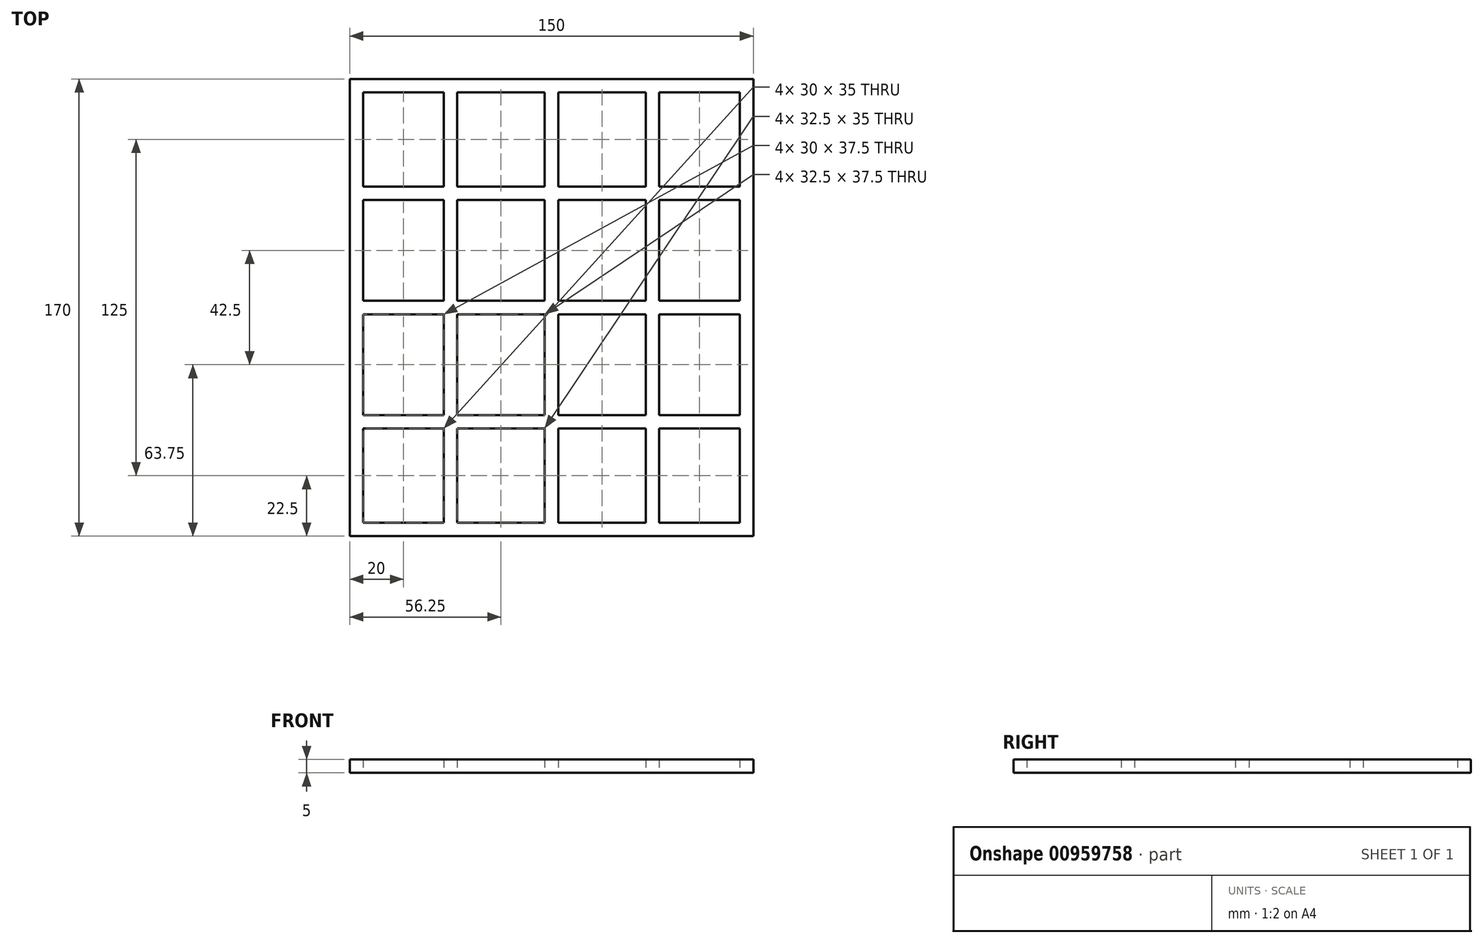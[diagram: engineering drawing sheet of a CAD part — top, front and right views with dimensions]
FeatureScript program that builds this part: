
annotation { "Feature Type Name" : "Feature", "Feature Type Description" : "" }
export const myFeature = defineFeature(function(context is Context, id is Id, definition is map)
    precondition{}
    {
        {
            var Q0;
            Q0=qCreatedBy(makeId("Top.planeOp"),FACE);
            var sketch = newSketch(context, id + "F0", { "sketchPlane" : qUnion([Q0])});
            skLineSegment(sketch, "E0.bottom", {"start": v(-107, 117) * mm, "end": v(107, 117) * mm});
            skLineSegment(sketch, "E0.top", {"start": v(-107, -117) * mm, "end": v(107, -117) * mm});
            skLineSegment(sketch, "E0.left", {"start": v(-107, 117) * mm, "end": v(-107, -117) * mm});
            skLineSegment(sketch, "E0.right", {"start": v(107, 117) * mm, "end": v(107, -117) * mm});
            skLineSegment(sketch, "E1.0", {"start": v(-75, 85) * mm, "end": v(-37.5, 85) * mm});
            skLineSegment(sketch, "E1.1", {"start": v(-75, 85) * mm, "end": v(-75, 42.5) * mm});
            skLineSegment(sketch, "E1.2", {"start": v(-75, -85) * mm, "end": v(-37.5, -85) * mm});
            skLineSegment(sketch, "E1.3", {"start": v(75, 85) * mm, "end": v(75, 42.5) * mm});
            skLineSegment(sketch, "E2", {"start": v(-75, 0) * mm, "end": v(-75, -42.5) * mm});
            skLineSegment(sketch, "E3", {"start": v(75, 0) * mm, "end": v(75, -42.5) * mm});
            skLineSegment(sketch, "E4", {"start": v(0, 85) * mm, "end": v(37.5, 85) * mm});
            skLineSegment(sketch, "E5", {"start": v(0, -85) * mm, "end": v(37.5, -85) * mm});
            skLineSegment(sketch, "E6", {"start": v(-37.5, -85) * mm, "end": v(0, -85) * mm});
            skLineSegment(sketch, "E7", {"start": v(37.5, -85) * mm, "end": v(75, -85) * mm});
            skLineSegment(sketch, "E8", {"start": v(75, 42.5) * mm, "end": v(75, 0) * mm});
            skLineSegment(sketch, "E9", {"start": v(75, -42.5) * mm, "end": v(75, -85) * mm});
            skLineSegment(sketch, "E10", {"start": v(-75, 42.5) * mm, "end": v(-75, 0) * mm});
            skLineSegment(sketch, "E11", {"start": v(-75, -42.5) * mm, "end": v(-75, -85) * mm});
            skLineSegment(sketch, "E12", {"start": v(37.5, 85) * mm, "end": v(75, 85) * mm});
            skLineSegment(sketch, "E13", {"start": v(-37.5, 85) * mm, "end": v(0, 85) * mm});
            skLineSegment(sketch, "E14.0", {"start": v(-70, 80) * mm, "end": v(-70, 45) * mm});
            skLineSegment(sketch, "E14.1", {"start": v(-70, 40) * mm, "end": v(-70, 2.5) * mm});
            skLineSegment(sketch, "E14.2", {"start": v(-70, -2.5) * mm, "end": v(-70, -40) * mm});
            skLineSegment(sketch, "E14.3", {"start": v(-70, -45) * mm, "end": v(-70, -80) * mm});
            skLineSegment(sketch, "E14.4", {"start": v(-70, -80) * mm, "end": v(-40, -80) * mm});
            skLineSegment(sketch, "E14.5", {"start": v(70, 80) * mm, "end": v(70, 45) * mm});
            skLineSegment(sketch, "E14.6", {"start": v(40, 80) * mm, "end": v(70, 80) * mm});
            skLineSegment(sketch, "E14.7", {"start": v(2.5, 80) * mm, "end": v(35, 80) * mm});
            skLineSegment(sketch, "E14.8", {"start": v(-35, 80) * mm, "end": v(-2.5, 80) * mm});
            skLineSegment(sketch, "E14.9", {"start": v(70, 40) * mm, "end": v(70, 2.5) * mm});
            skLineSegment(sketch, "E14.10", {"start": v(70, -2.5) * mm, "end": v(70, -40) * mm});
            skLineSegment(sketch, "E14.11", {"start": v(70, -45) * mm, "end": v(70, -80) * mm});
            skLineSegment(sketch, "E14.12", {"start": v(40, -80) * mm, "end": v(70, -80) * mm});
            skLineSegment(sketch, "E14.13", {"start": v(2.5, -80) * mm, "end": v(35, -80) * mm});
            skLineSegment(sketch, "E14.14", {"start": v(-70, 80) * mm, "end": v(-40, 80) * mm});
            skLineSegment(sketch, "E14.15", {"start": v(-35, -80) * mm, "end": v(-2.5, -80) * mm});
            skLineSegment(sketch, "E15.0", {"start": v(-40, -45) * mm, "end": v(-40, -80) * mm});
            skLineSegment(sketch, "E15.1", {"start": v(-40, -2.5) * mm, "end": v(-40, -40) * mm});
            skLineSegment(sketch, "E15.2", {"start": v(-40, 40) * mm, "end": v(-40, 2.5) * mm});
            skLineSegment(sketch, "E15.3", {"start": v(-40, 80) * mm, "end": v(-40, 45) * mm});
            skLineSegment(sketch, "E16.0", {"start": v(-35, -45) * mm, "end": v(-35, -80) * mm});
            skLineSegment(sketch, "E16.1", {"start": v(-35, -2.5) * mm, "end": v(-35, -40) * mm});
            skLineSegment(sketch, "E16.2", {"start": v(-35, 40) * mm, "end": v(-35, 2.5) * mm});
            skLineSegment(sketch, "E16.3", {"start": v(-35, 80) * mm, "end": v(-35, 45) * mm});
            skLineSegment(sketch, "E17.0", {"start": v(-2.5, -45) * mm, "end": v(-2.5, -80) * mm});
            skLineSegment(sketch, "E17.1", {"start": v(-2.5, -2.5) * mm, "end": v(-2.5, -40) * mm});
            skLineSegment(sketch, "E17.2", {"start": v(-2.5, 40) * mm, "end": v(-2.5, 2.5) * mm});
            skLineSegment(sketch, "E17.3", {"start": v(-2.5, 80) * mm, "end": v(-2.5, 45) * mm});
            skLineSegment(sketch, "E18.0", {"start": v(2.5, -45) * mm, "end": v(2.5, -80) * mm});
            skLineSegment(sketch, "E18.1", {"start": v(2.5, -2.5) * mm, "end": v(2.5, -40) * mm});
            skLineSegment(sketch, "E18.2", {"start": v(2.5, 40) * mm, "end": v(2.5, 2.5) * mm});
            skLineSegment(sketch, "E18.3", {"start": v(2.5, 80) * mm, "end": v(2.5, 45) * mm});
            skLineSegment(sketch, "E19.0", {"start": v(35, -45) * mm, "end": v(35, -80) * mm});
            skLineSegment(sketch, "E19.1", {"start": v(35, -2.5) * mm, "end": v(35, -40) * mm});
            skLineSegment(sketch, "E19.2", {"start": v(35, 40) * mm, "end": v(35, 2.5) * mm});
            skLineSegment(sketch, "E19.3", {"start": v(35, 80) * mm, "end": v(35, 45) * mm});
            skLineSegment(sketch, "E20.0", {"start": v(40, -45) * mm, "end": v(40, -80) * mm});
            skLineSegment(sketch, "E20.1", {"start": v(40, -2.5) * mm, "end": v(40, -40) * mm});
            skLineSegment(sketch, "E20.2", {"start": v(40, 40) * mm, "end": v(40, 2.5) * mm});
            skLineSegment(sketch, "E20.3", {"start": v(40, 80) * mm, "end": v(40, 45) * mm});
            skLineSegment(sketch, "E21.0", {"start": v(40, 40) * mm, "end": v(70, 40) * mm});
            skLineSegment(sketch, "E21.1", {"start": v(2.5, 40) * mm, "end": v(35, 40) * mm});
            skLineSegment(sketch, "E21.2", {"start": v(-35, 40) * mm, "end": v(-2.5, 40) * mm});
            skLineSegment(sketch, "E21.3", {"start": v(-70, 40) * mm, "end": v(-40, 40) * mm});
            skLineSegment(sketch, "E22.0", {"start": v(40, 45) * mm, "end": v(70, 45) * mm});
            skLineSegment(sketch, "E22.1", {"start": v(2.5, 45) * mm, "end": v(35, 45) * mm});
            skLineSegment(sketch, "E22.2", {"start": v(-35, 45) * mm, "end": v(-2.5, 45) * mm});
            skLineSegment(sketch, "E22.3", {"start": v(-70, 45) * mm, "end": v(-40, 45) * mm});
            skLineSegment(sketch, "E23.0", {"start": v(40, -2.5) * mm, "end": v(70, -2.5) * mm});
            skLineSegment(sketch, "E23.1", {"start": v(2.5, -2.5) * mm, "end": v(35, -2.5) * mm});
            skLineSegment(sketch, "E23.2", {"start": v(-35, -2.5) * mm, "end": v(-2.5, -2.5) * mm});
            skLineSegment(sketch, "E23.3", {"start": v(-70, -2.5) * mm, "end": v(-40, -2.5) * mm});
            skLineSegment(sketch, "E24.0", {"start": v(40, 2.5) * mm, "end": v(70, 2.5) * mm});
            skLineSegment(sketch, "E24.1", {"start": v(2.5, 2.5) * mm, "end": v(35, 2.5) * mm});
            skLineSegment(sketch, "E24.2", {"start": v(-35, 2.5) * mm, "end": v(-2.5, 2.5) * mm});
            skLineSegment(sketch, "E24.3", {"start": v(-70, 2.5) * mm, "end": v(-40, 2.5) * mm});
            skLineSegment(sketch, "E25.0", {"start": v(40, -45) * mm, "end": v(70, -45) * mm});
            skLineSegment(sketch, "E25.1", {"start": v(2.5, -45) * mm, "end": v(35, -45) * mm});
            skLineSegment(sketch, "E25.2", {"start": v(-35, -45) * mm, "end": v(-2.5, -45) * mm});
            skLineSegment(sketch, "E25.3", {"start": v(-70, -45) * mm, "end": v(-40, -45) * mm});
            skLineSegment(sketch, "E26.0", {"start": v(40, -40) * mm, "end": v(70, -40) * mm});
            skLineSegment(sketch, "E26.1", {"start": v(2.5, -40) * mm, "end": v(35, -40) * mm});
            skLineSegment(sketch, "E26.2", {"start": v(-35, -40) * mm, "end": v(-2.5, -40) * mm});
            skLineSegment(sketch, "E26.3", {"start": v(-70, -40) * mm, "end": v(-40, -40) * mm});
            skPoint(sketch, "E27.orphan", {"position": v(-75, 42.5) * mm});
            skPoint(sketch, "E28.trimOffspring.end.orphan", {"position": v(75, 42.5) * mm});
            skPoint(sketch, "E29.trimOffspring.end.orphan", {"position": v(37.5, 42.5) * mm});
            skPoint(sketch, "E30.start.orphan", {"position": v(0, 42.5) * mm});
            skPoint(sketch, "E31.orphan", {"position": v(37.5, 0) * mm});
            skPoint(sketch, "E32.orphan", {"position": v(0, 0) * mm});
            skPoint(sketch, "E33.end.orphan", {"position": v(75, 0) * mm});
            skPoint(sketch, "E34.orphan", {"position": v(-75, 0) * mm});
            skPoint(sketch, "E35.orphan", {"position": v(-37.5, 0) * mm});
            skPoint(sketch, "E36.orphan", {"position": v(-75, -42.5) * mm});
            skPoint(sketch, "E37.end.orphan", {"position": v(-37.5, -42.5) * mm});
            skPoint(sketch, "E38.end.orphan", {"position": v(-37.5, -85) * mm});
            skPoint(sketch, "E39.orphan", {"position": v(0, -85) * mm});
            skPoint(sketch, "E40.end.orphan", {"position": v(0, -42.5) * mm});
            skPoint(sketch, "E41.end.orphan", {"position": v(37.5, -42.5) * mm});
            skPoint(sketch, "E42.end.orphan", {"position": v(75, -42.5) * mm});
            skPoint(sketch, "E43.end.orphan", {"position": v(37.5, -85) * mm});
            skPoint(sketch, "E44.start.orphan", {"position": v(37.5, 85) * mm});
            skPoint(sketch, "E45.start.orphan", {"position": v(0, 85) * mm});
            skPoint(sketch, "E46.start.orphan", {"position": v(-37.5, 42.5) * mm});
            skPoint(sketch, "E47.start.orphan", {"position": v(-37.5, 85) * mm});
            skSolve(sketch);
        }
        {
            var Q0;
            Q0=makeQuery(id+"F0.imprint","IMPRINT",FACE,{"disambiguationData":[TD([[makeQuery(id+"F0.imprint","IMPRINT",EDGE,{"derivedFrom":sQuery(id+"F0.wireOp",EDGE,"E1.0")}),-1.0]])]});
            extrude(context, id + "F1", {"entities" : qUnion([Q0]), "depth" : 5 * mm, "offsetDistance" : 25 * mm});
        }
    });
